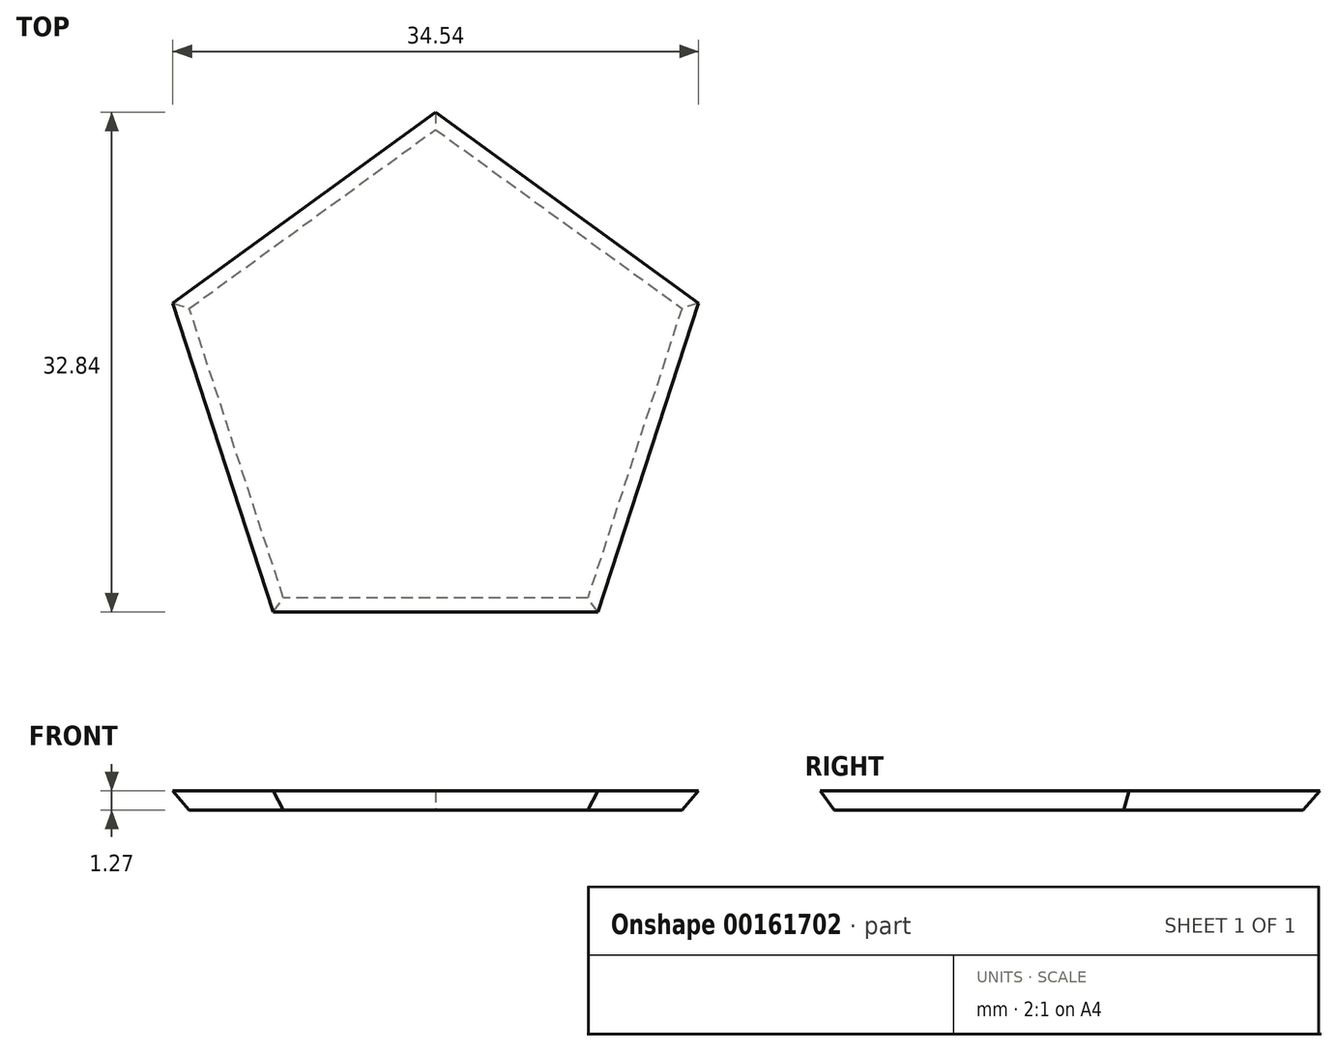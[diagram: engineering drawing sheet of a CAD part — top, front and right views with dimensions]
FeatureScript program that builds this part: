
annotation { "Feature Type Name" : "Feature", "Feature Type Description" : "" }
export const myFeature = defineFeature(function(context is Context, id is Id, definition is map)
    precondition{}
    {
        {
            var Q0;
            Q0=qCreatedBy(makeId("Top.planeOp"),FACE);
            var sketch = newSketch(context, id + "F0", { "sketchPlane" : qUnion([Q0])});
            skCircle(sketch, "E0.cCircle", {"center": v(0, 0) * mm, "radius": 17.01 * mm, "construction": true});
            skLineSegment(sketch, "E0.0", {"start": v(16.18, 5.26) * mm, "end": v(10, -13.76) * mm});
            skLineSegment(sketch, "E0.1", {"start": v(10, -13.76) * mm, "end": v(-10, -13.76) * mm});
            skLineSegment(sketch, "E0.2", {"start": v(-10, -13.76) * mm, "end": v(-16.18, 5.26) * mm});
            skLineSegment(sketch, "E0.3", {"start": v(-16.18, 5.26) * mm, "end": v(0, 17.01) * mm});
            skLineSegment(sketch, "E0.4", {"start": v(0, 17.01) * mm, "end": v(16.18, 5.26) * mm});
            skSolve(sketch);
        }
        {
            var Q0;
            Q0=makeQuery(id+"F0.imprint","IMPRINT",FACE,{"disambiguationData":[TD([[makeQuery(id+"F0.imprint","IMPRINT",EDGE,{"derivedFrom":sQuery(id+"F0.wireOp",EDGE,"E0.0")}),-1.0]])]});
            extrude(context, id + "F1", {"entities" : qUnion([Q0]), "depth" : 1.27 * mm, "hasDraft" : true, "draftAngle" : 36 * degree});
        }
    });
